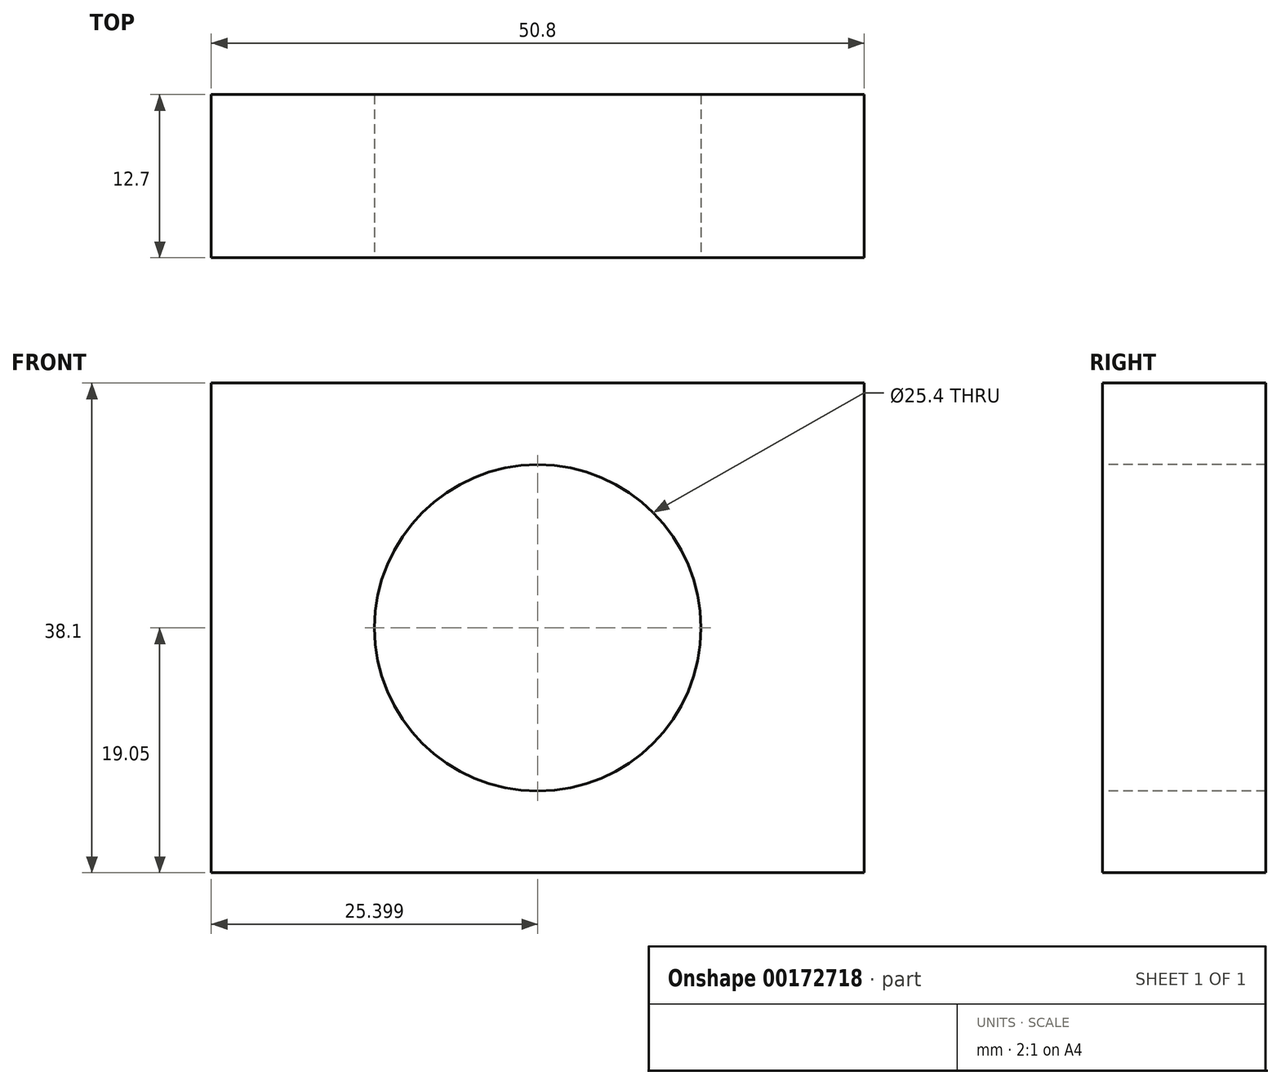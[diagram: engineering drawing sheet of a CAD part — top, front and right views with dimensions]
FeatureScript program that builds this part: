
annotation { "Feature Type Name" : "Feature", "Feature Type Description" : "" }
export const myFeature = defineFeature(function(context is Context, id is Id, definition is map)
    precondition{}
    {
        {
            var Q0;
            Q0=qCreatedBy(makeId("Front.planeOp"),FACE);
            var sketch = newSketch(context, id + "F0", { "sketchPlane" : qUnion([Q0])});
            skLineSegment(sketch, "E0.bottom", {"start": v(-30.06, 38.1) * mm, "end": v(20.74, 38.1) * mm});
            skLineSegment(sketch, "E0.top", {"start": v(-30.06, 0) * mm, "end": v(20.74, 0) * mm});
            skLineSegment(sketch, "E0.left", {"start": v(-30.06, 38.1) * mm, "end": v(-30.06, 0) * mm});
            skLineSegment(sketch, "E0.right", {"start": v(20.74, 38.1) * mm, "end": v(20.74, 0) * mm});
            skSolve(sketch);
        }
        {
            var Q0;
            Q0=makeQuery(id+"F0.imprint","IMPRINT",FACE,{"disambiguationData":[TD([[makeQuery(id+"F0.imprint","IMPRINT",EDGE,{"derivedFrom":sQuery(id+"F0.wireOp",EDGE,"E0.bottom")}),-1.0]])]});
            extrude(context, id + "F1", {"entities" : qUnion([Q0]), "depth" : 12.7 * mm});
        }
        {
            var Q0;
            Q0=makeQuery(id+"F1.opExtrude","CAP_FACE",FACE,{"disambiguationData":[OSD([sQuery(id+"F0.wireOp",EDGE,"E0.bottom"),sQuery(id+"F0.wireOp",EDGE,"E0.top"),sQuery(id+"F0.wireOp",EDGE,"E0.left"),sQuery(id+"F0.wireOp",EDGE,"E0.right")])],"isStart":false});
            var sketch = newSketch(context, id + "F2", { "sketchPlane" : qUnion([Q0])});
            skCircle(sketch, "E1", {"center": v(-4.66, 19.05) * mm, "radius": 12.7 * mm});
            skPoint(sketch, "E1.centerSnap0", {"position": v(-4.66, 0) * mm});
            skSolve(sketch);
        }
        {
            var Q0;
            Q0=sQuery(id+"F2.wireOp",VERTEX,"E1.center");
            var Q1;
            Q1=makeQuery(id+"F1.opExtrude","SWEPT_BODY",BODY,{"disambiguationData":[OSD([sQuery(id+"F0.wireOp",EDGE,"E0.bottom"),sQuery(id+"F0.wireOp",EDGE,"E0.top"),sQuery(id+"F0.wireOp",EDGE,"E0.left"),sQuery(id+"F0.wireOp",EDGE,"E0.right")])]});
            hole(context, id + "F3", {"style" : HoleStyle.SIMPLE, "endStyle" : HoleEndStyle.THROUGH, "holeDiameter" : 25.4 * mm, "locations" : qUnion([Q0]), "scope" : qUnion([Q1]), "isTappedThrough" : true});
        }
    });
